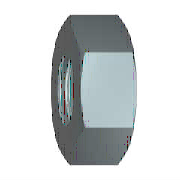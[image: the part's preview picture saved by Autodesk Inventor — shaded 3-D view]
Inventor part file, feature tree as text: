
AUTODESK INVENTOR PART (.ipt)
format: ipt  version: 2015 (Build 190159000, 159)  size: 161,792 bytes
history: native  units: mm (DEFAULTED — no unit token found)
features: sketch x3, chamfer x1, hole x1, other x1, plane x1
ambient origin geometry x7: Origin, YZ Plane, XZ Plane, X Axis, Y Axis, Z Axis, Center Point
bodies: Solid1 (feature_tree), Body (feature_tree)
feature tree (7):
  chamfer  "Chamfer1"  Angle=30.0deg  [1 undecoded]
  hole  "Thread"  [1 undecoded]
  other  "Work Axis1"
  plane  "Work Plane1"
  sketch  "Sketch1"  dims[d0=4.618802mm]
  sketch  "Sketch2"  dims[d1=1.6mm]
  sketch  "Sketch3"  dims[d2=0.0mm d3=30.0deg d4=30.0deg d5=3.1mm d6=3.1mm d7=90.0deg d25=1.567mm d26=6.0mm d27=4.0mm d28=2.0mm d29=14.3117mm d30=8.0mm d31=20.594885mm d8=0.216506mm d9=30.0deg d10=0.216506mm d11=30.0deg d13=0.0mm d14=0.0mm d39=0.0mm d40=0.216506mm d41=0.216506mm d42=0.0mm]
note: 2 required parameter values undecoded (feature->parameter linkage not recoverable at this tier; creation-order binding heuristic only, values carry confidence <= 0.55)
